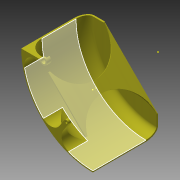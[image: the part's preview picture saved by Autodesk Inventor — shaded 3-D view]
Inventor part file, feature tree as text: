
AUTODESK INVENTOR PART (.ipt)
format: ipt  version: 2015 (Build 190159000, 159)  size: 874,496 bytes
history: native  units: mm
features: sketch x24, extrude x20, fillet x6, revolve x5, mirror x1
ambient origin geometry x8: Origin, YZ Plane, XZ Plane, XY Plane, X Axis, Y Axis, Z Axis, Center Point
bodies: Body1 (feature_tree)
feature tree (56):
  sketch  "Boceto1"  dims[d1=40.0mm d2=20.0mm d3=20.0mm d4=5.0mm d5=360.0deg d6=5.0mm d7=5.0mm d9=5.0mm d10=10.0mm d11=2.451216mm d13=270.0mm]
  revolve  "Revolución1"  [1 undecoded]
  sketch  "Boceto3"  dims[d20=3.0mm d21=120.0mm]
  extrude  "Extrusión2"  Depth=100.0mm
  extrude  "Extrusión3"  Depth=120.0mm
  sketch  "Boceto6"  dims[d22=3.0mm d23=120.0mm]
  revolve  "Revolución2"  [1 undecoded]
  revolve  "Revolución3"  [1 undecoded]
  revolve  "Revolución4"  [1 undecoded]
  revolve  "Revolución5"  [1 undecoded]
  fillet  "Empalme2"  Radius=100.0mm
  sketch  "Boceto7"  dims[d24=90.0deg]
  extrude  "Extrusión7"  Depth=20.0mm
  extrude  "Extrusión8"  Depth=3.0mm
  extrude  "Extrusión9"  TaperAngle=90.0deg  [1 undecoded]
  extrude  "Extrusión10"  TaperAngle=90.0deg  [1 undecoded]
  fillet  "Empalme4"  Radius=3.0mm
  fillet  "Empalme5"  Radius=20.0mm
  sketch  "Boceto16"  dims[d57=135.0mm d58=3.0mm]
  extrude  "Extrusión11"  Depth=10.0mm
  extrude  "Extrusión12"  Depth=10.0mm TaperAngle=0.0deg
  extrude  "Extrusión13"  Depth=8.0mm
  extrude  "Extrusión14"  Depth=8.0mm
  extrude  "Extrusión15"  Depth=20.0mm TaperAngle=360.0deg
  extrude  "Extrusión16"  Depth=6.0mm TaperAngle=0.0deg
  mirror  "Simetría1"
  extrude  "Extrusión17"  Depth=30.0mm
  extrude  "Extrusión18"  Depth=1220.0mm TaperAngle=0.0deg
  sketch  "Boceto25"  dims[d95=30.0mm d96=20.0mm]
  sketch  "Boceto26"  dims[d97=60.0deg d98=1220.0mm d99=0.0mm]
  extrude  "Extrusión19"  Depth=6.0mm TaperAngle=0.0deg
  extrude  "Extrusión20"  TaperAngle=45.0deg  [1 undecoded]
  extrude  "Extrusión21"  Depth=10.0mm TaperAngle=0.0deg
  sketch  "Boceto27"  dims[d100=888.0mm d101=0.0mm d102=6.0mm d103=0.0mm]
  extrude  "Extrusión22"  Depth=30.0mm TaperAngle=0.0deg
  extrude  "Extrusión23"  Depth=30.0mm TaperAngle=0.0deg
  fillet  "Empalme7"  Radius=3.0mm
  fillet  "Empalme8"  Radius=12.0mm
  extrude  "Extrusión24"  Depth=30.0mm TaperAngle=0.0deg
  fillet  "Empalme9"  Radius=3.0mm
  sketch  "Boceto2"  dims[d14=3.0mm d19=100.0mm]
  sketch  "Boceto11"  dims[d26=40.0mm d27=20.0mm d28=20.0mm d29=5.0mm d30=360.0deg d31=5.0mm d32=5.0mm d33=5.0mm d34=10.0mm d35=2.451216mm d36=270.0mm d37=3.0mm d38=60.0mm d39=0.0mm]
  sketch  "Boceto12"  dims[d40=3.0mm d41=0.0mm d51=20.0mm]
  sketch  "Boceto13"  dims[d52=45.0mm d53=20.0mm d54=100.0mm]
  sketch  "Boceto14"  dims[d55=90.0deg d56=20.0mm]
  sketch  "Boceto17"  dims[d59=90.0deg d60=90.0deg]
  sketch  "Boceto18"  dims[d61=90.0deg d62=90.0deg d63=3.0mm d69=20.0mm]
  sketch  "Boceto19"  dims[d70=10.0mm d71=10.0mm]
  sketch  "Boceto20"  dims[d73=10.0mm d74=111.0mm d75=0.0mm]
  sketch  "Boceto21"  dims[d79=8.0mm d80=8.0mm]
  sketch  "Boceto22"  dims[d81=8.0mm d82=8.0mm]
  sketch  "Boceto23"  dims[d83=6.0mm d84=0.0mm d87=20.0mm d89=360.0deg]
  sketch  "Boceto24"  dims[d91=6.0mm d92=0.0mm d93=6.0mm d94=0.0mm]
  sketch  "Boceto28"  dims[d106=1.0mm d107=0.0mm d108=45.0deg]
  sketch  "Boceto29"  dims[d109=3.0mm d110=10.0mm d111=0.0mm]
  sketch  "Boceto30"  dims[d114=2.0mm d115=0.0mm d116=6.0mm d117=0.0mm d118=6.0mm d119=0.0mm d120=3.0mm d121=12.0mm d122=0.0mm d123=6.0mm d124=0.0mm d125=3.0mm d126=0.0mm d127=30.0deg d128=6.0mm d129=0.0mm d130=6.0mm d131=0.0mm d132=2.0mm d133=1.0mm d134=9.0mm d135=6.0mm d136=0.0mm d137=30.0mm]
note: 8 required parameter values undecoded (feature->parameter linkage not recoverable at this tier; creation-order binding heuristic only, values carry confidence <= 0.55)